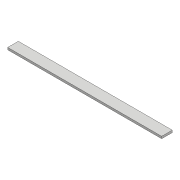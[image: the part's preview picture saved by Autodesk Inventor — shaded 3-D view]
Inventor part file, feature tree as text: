
AUTODESK INVENTOR PART (.ipt)
format: ipt  version: 2017 (Build 210142000, 142)  size: 70,656 bytes
history: native  units: mm
features: extrude x1, sketch x1
ambient origin geometry x8: Origin, YZ Plane, XZ Plane, XY Plane, X Axis, Y Axis, Z Axis, Center Point
bodies: Solid1 (feature_tree)
feature tree (2):
  extrude  "Extrusion1"  Depth=50.0mm
  sketch  "Sketch1"  dims[d0=725.0mm d1=50.0mm d2=10.0mm d3=0.0mm]
